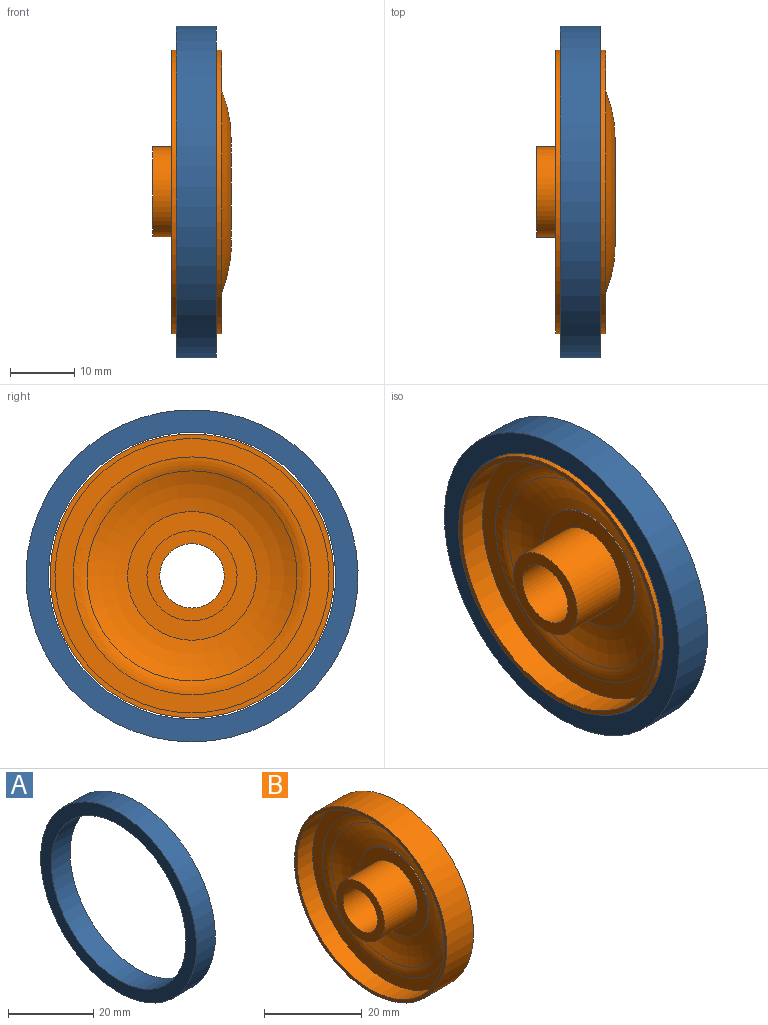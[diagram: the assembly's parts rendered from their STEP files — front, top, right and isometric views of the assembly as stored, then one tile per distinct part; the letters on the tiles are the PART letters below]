
ASSEMBLY  parts=2 mates=1
PART A: 4 faces, bbox 6.2x51.6x51.6 mm
  f0: cylinder r=22.3mm len=44.6mm, axis (-1,0,0), area 872.9mm2, adj f2,f3
  f1: cylinder r=25.8mm len=51.6mm, axis (-1,0,0), area 1009.9mm2, adj f2,f3
  f2: plane 51.6x51.6mm, normal (1,0,0), area 528.9mm2, adj f0,f1
  f3: plane 51.6x51.6mm, normal (-1,0,0), area 528.9mm2, adj f0,f1
PART B: 17 faces, bbox 12.2x44.1x44.1 mm
  f0: cylinder r=18.4mm len=36.8mm, axis (1,0,0), area 57.8mm2, adj f1,f15
  f1: plane 42.6x42.6mm, normal (1,0,0), area 361.7mm2, adj f0,f2
  f2: cylinder r=21.3mm len=42.6mm, axis (1,0,0), area 100.4mm2, adj f1,f3
  f3: plane 44.1x44.1mm, normal (1,0,0), area 102.1mm2, adj f2,f4
  f4: cylinder r=22.05mm len=44.1mm, axis (1,0,0), area 1070.9mm2, adj f3,f5
  f5: plane 44.1x44.1mm, normal (-1,0,0), area 102.1mm2, adj f4,f6
  f6: cylinder r=21.3mm len=42.6mm, axis (1,0,0), area 602.2mm2, adj f5,f7
  f7: plane 42.6x42.6mm, normal (-1,0,0), area 353.1mm2, adj f6,f16
  f8: torus R=7.72mm, axis (1,0,0), area 547.6mm2, adj f9,f16
  f9: cylinder r=10mm len=20mm, axis (1,0,0), area 15.7mm2, adj f8,f10
  f10: plane 20x20mm, normal (-1,0,0), area 160.2mm2, adj f9,f11
  f11: cylinder r=7mm len=14mm, axis (1,0,0), area 420.7mm2, adj f10,f12
  f12: plane 14x14mm, normal (-1,0,0), area 75.4mm2, adj f11,f13
  f13: cylinder r=5mm len=12.23mm, axis (1,0,0), area 384.1mm2, adj f12,f14
  f14: plane 15.44x15.44mm, normal (1,0,0), area 108.7mm2, adj f13,f15
  f15: torus R=7.72mm, axis (1,0,0), area 922.6mm2, adj f0,f14
  f16: torus R=18.47mm, axis (-1,0,0), area 244.1mm2, adj f7,f8
PLACE A t=(-30.83,-10.27,12.83)mm
PLACE B t=(-30.72,-10.27,12.83)mm
MATE cylindrical A.f0 <-> B.f0  axis (-1,0,0) through (-30.83,-10.27,12.83)mm
